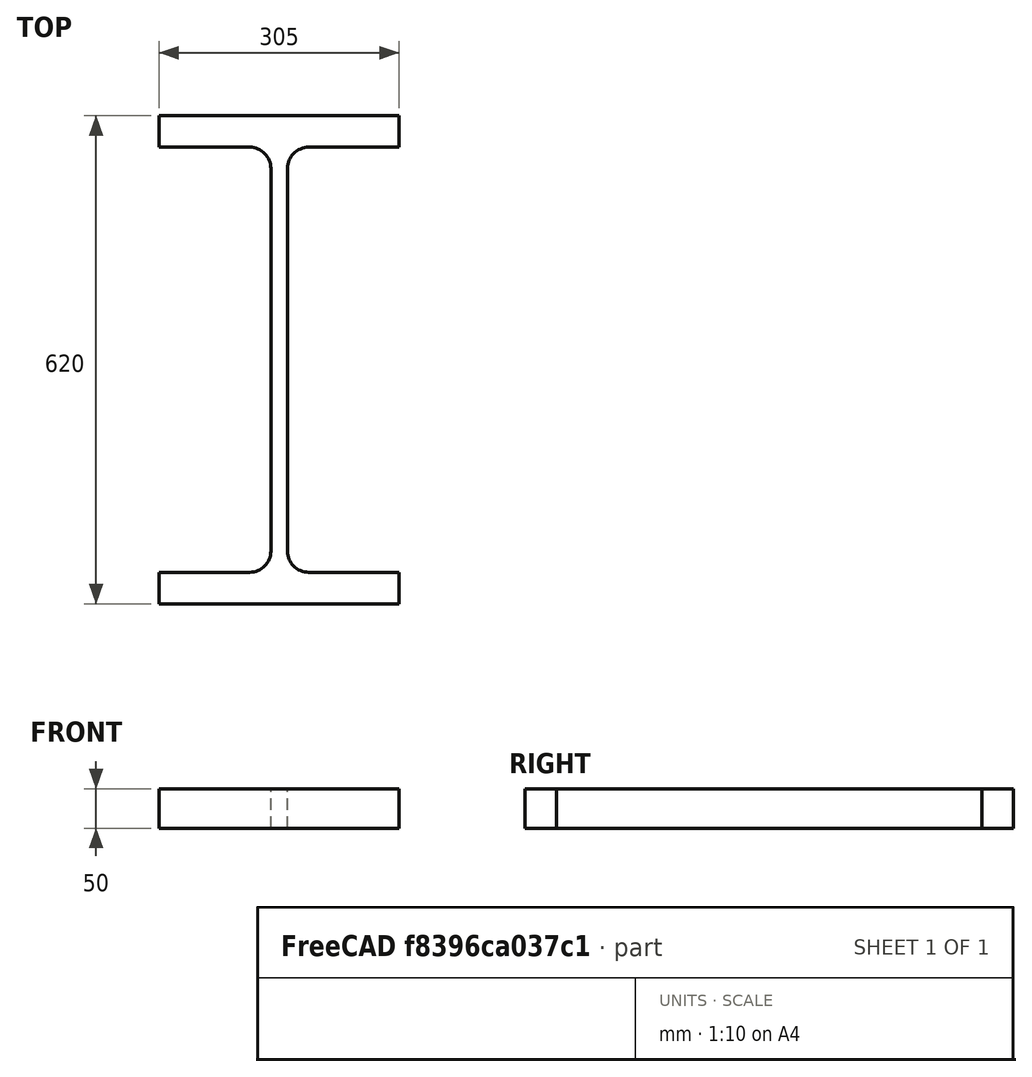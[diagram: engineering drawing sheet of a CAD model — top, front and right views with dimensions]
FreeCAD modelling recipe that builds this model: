
FCSTD DOCUMENT  (FreeCAD 0.15R4671 (Git))
Label: HE-M-Profile 600 DIN1025-4 S235JR
License: All rights reserved
LicenseURL: http://en.wikipedia.org/wiki/All_rights_reserved
objects: Sketcher::SketchObject×1, Part::Extrusion×1
note: 2 computed .brp shape members not serialized (recipe doc carries the construction recipe); baked Part::Feature solids carry a one-line shape summary decoded from their .brp

FEATURE [Sketcher::SketchObject] Sketch
  sketch-geometry (16):
    g0: LineSegment StartX=10.5 StartY=-243 StartZ=0 EndX=10.5 EndY=243 EndZ=0
    g1: LineSegment StartX=37.5 StartY=270 StartZ=0 EndX=152.5 EndY=270 EndZ=0
    g2: LineSegment StartX=152.5 StartY=270 StartZ=0 EndX=152.5 EndY=310 EndZ=0
    g3: LineSegment StartX=152.5 StartY=310 StartZ=0 EndX=-152.5 EndY=310 EndZ=0
    g4: LineSegment StartX=-152.5 StartY=310 StartZ=0 EndX=-152.5 EndY=270 EndZ=0
    g5: LineSegment StartX=-152.5 StartY=270 StartZ=0 EndX=-37.5 EndY=270 EndZ=0
    g6: LineSegment StartX=-10.5 StartY=243 StartZ=0 EndX=-10.5 EndY=-243 EndZ=0
    g7: LineSegment StartX=-37.5 StartY=-270 StartZ=0 EndX=-152.5 EndY=-270 EndZ=0
    g8: LineSegment StartX=-152.5 StartY=-270 StartZ=0 EndX=-152.5 EndY=-310 EndZ=0
    g9: LineSegment StartX=-152.5 StartY=-310 StartZ=0 EndX=152.5 EndY=-310 EndZ=0
    g10: LineSegment StartX=152.5 StartY=-310 StartZ=0 EndX=152.5 EndY=-270 EndZ=0
    g11: LineSegment StartX=152.5 StartY=-270 StartZ=0 EndX=37.5 EndY=-270 EndZ=0
    g12: ArcOfCircle CenterX=37.5 CenterY=243 CenterZ=0 NormalX=0 NormalY=0 NormalZ=1 Radius=27 StartAngle=1.5708 EndAngle=3.14159
    g13: ArcOfCircle CenterX=37.5 CenterY=-243 CenterZ=0 NormalX=0 NormalY=0 NormalZ=1 Radius=27 StartAngle=3.14159 EndAngle=4.71239
    g14: ArcOfCircle CenterX=-37.5 CenterY=243 CenterZ=0 NormalX=0 NormalY=0 NormalZ=1 Radius=27 StartAngle=0 EndAngle=1.5708
    g15: ArcOfCircle CenterX=-37.5 CenterY=-243 CenterZ=0 NormalX=0 NormalY=0 NormalZ=1 Radius=27 StartAngle=4.71239 EndAngle=6.28319
  constraints (42):
    c: Vertical(g0)
    c: Coincident(g2,g1)
    c: Vertical(g2)
    c: Coincident(g3,g2)
    c: Coincident(g4,g3)
    c: Vertical(g4)
    c: Coincident(g5,g4)
    c: Horizontal(g5)
    c: Vertical(g6)
    c: Horizontal(g7)
    c: Coincident(g8,g7)
    c: Vertical(g8)
    c: Coincident(g9,g8)
    c: Horizontal(g9)
    c: Coincident(g10,g9)
    c: Vertical(g10)
    c: Coincident(g11,g10)
    c: Horizontal(g11)
    c: Tangent(g1,g12) = 1.5708
    c: Tangent(g0,g12) = 1.5708
    c: Tangent(g0,g13) = 1.5708
    c: Tangent(g11,g13) = 1.5708
    c: Tangent(g5,g14) = 1.5708
    c: Tangent(g6,g14) = 1.5708
    c: Tangent(g6,g15) = 1.5708
    c: Tangent(g7,g15) = 1.5708
    c: Equal(g3,g9)
    c: Equal(g2,g4)
    c: Equal(g4,g8)
    c: Equal(g8,g10)
    c: Equal(g12,g14)
    c: Equal(g14,g15)
    c: Equal(g15,g13)
    c: Symmetric(g2,g3,g-2)
    c: Symmetric(g9,g8,g-2)
    c: Symmetric(g0,g6,g-2)
    c: Symmetric(g2,g9,g-1)
    c: DistanceY(g2,g9) = -620
    c: DistanceX(g3) = -305
    c: DistanceX(g0,g6) = -21
    c: DistanceY(g2) = 40
    c: Radius(g12) = 27
FEATURE [Part::Extrusion] Extrude  label="HE-M-Profile 600 DIN1025-4 S235JR"
  Base = -> Sketch
  Dir = (0,0,50)
  Solid = true
